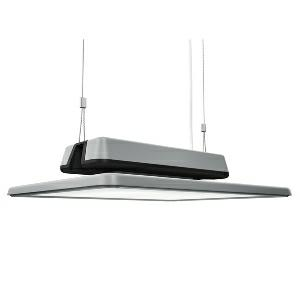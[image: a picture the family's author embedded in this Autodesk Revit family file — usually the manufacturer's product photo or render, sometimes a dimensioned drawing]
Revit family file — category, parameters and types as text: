
# Revit family: acaneo_-_hial_20000_840_n_ea_00734269_9d3b
name_source: partatom
category: Lighting Fixtures
units: mm (PartAtom-declared; Revit-internal decimal feet)

## family parameters
Cut with Voids When Loaded = No
Host = Face
Light Source = No
Part Type = Normal
Room Calculation Point = No
Round Connector Dimension = Use Diameter
Shared = No

## types (1)
- ACANEO - HIAL 20000/840/N/EA (1 x LED, 22000 lm, 4000K)
    Apparent Load = 140 VA
    Approval mark = CE
    CIE Flux Codes = 84 97 100 100 100
    Color Rendering = 80-89
    Color Temperature = 4000K
    Control Gear = Electronic ballast
    Default Elevation = 1800 mm
    Description = HIAL 20000/840/N/EA|High bay luminaire|light source: LED|work equipment: Electronic ballast|connected load: 220-240 V, 50/60 Hz|Power consumption: approx. 140 W|power factor: approx. 0,951|luminous flux: 22000 lm|luminous efficacy: 157 lm/W|colour temperature: Cold white, ca. 4000 K|color rendering index (CRI): >= 80|chromaticity tolerance:  3 SDCM|System of protection: IP 65|class of protection: I|technology: Switchable|luminaire body|material: Aluminium|surface: Powder coatet|colour: White aluminium|lamp cover: Acrylic (PMMA), Clear|weight (net): approx. 8.2 kg|mains lead: Built-in plug RST 25i3 Einbau|Fastening: Available separately|Accessory: Junction box (RST 2013)|minimum ambient temperature: -30 ░C|maximum ambient temperature: 50 ░C|glare control: Optics|unified glare rating(4H 8H): <=  22|
    Frequency = 50 Hz, 60 Hz
    Height = 125 mm
    Lamp = 1 x LED
    Lamp Light Flux = 22000 lm
    Lamp count = 1
    Length = 480 mm
    Luminous efficacy = 157 lm/W
    Manufacturer = Waldmann
    ModVariant = No
    Model = 00734269
    Mounting Place = Ceiling
    Mounting Type = Pendant
    Number of Poles = 1
    OnlyDefault = Yes
    Power Factor = 1
    Product Name = ACANEO - HIAL 20000/840/N/EA
    Product group = High bay luminaire (industry)
    ProductGroupID = 901
    Protection Class = Protection class I
    Protection Degree = IP 65
    RLX_Detail_Level = 1
    RLX_Emergency_Light_Flux = 0 lm
    RLX_Emergency_Type = 0
    RLX_Emergency_Type_DB = No
    RlxData = <blob elided: 30261 chars, md5=ae3b3022>
    Socket = socket
    Standby Power = 0 W
    System Light Flux = 22000 lm
    System Power = 140 W
    Type Comments = Product without accessories
    Type Image = acaneo-hial.jpg
    URL = http://relux.com
    VarID = ---
    Voltage = 230 V
    Voltage Range = 110-120 V, 220-240 V
    Weight = 0.00 kg
    Width = 405 mm

## geometry (parser evidence)
native form markers: Blend x4, Sweep x10
no freeform markers — native parametric forms only
